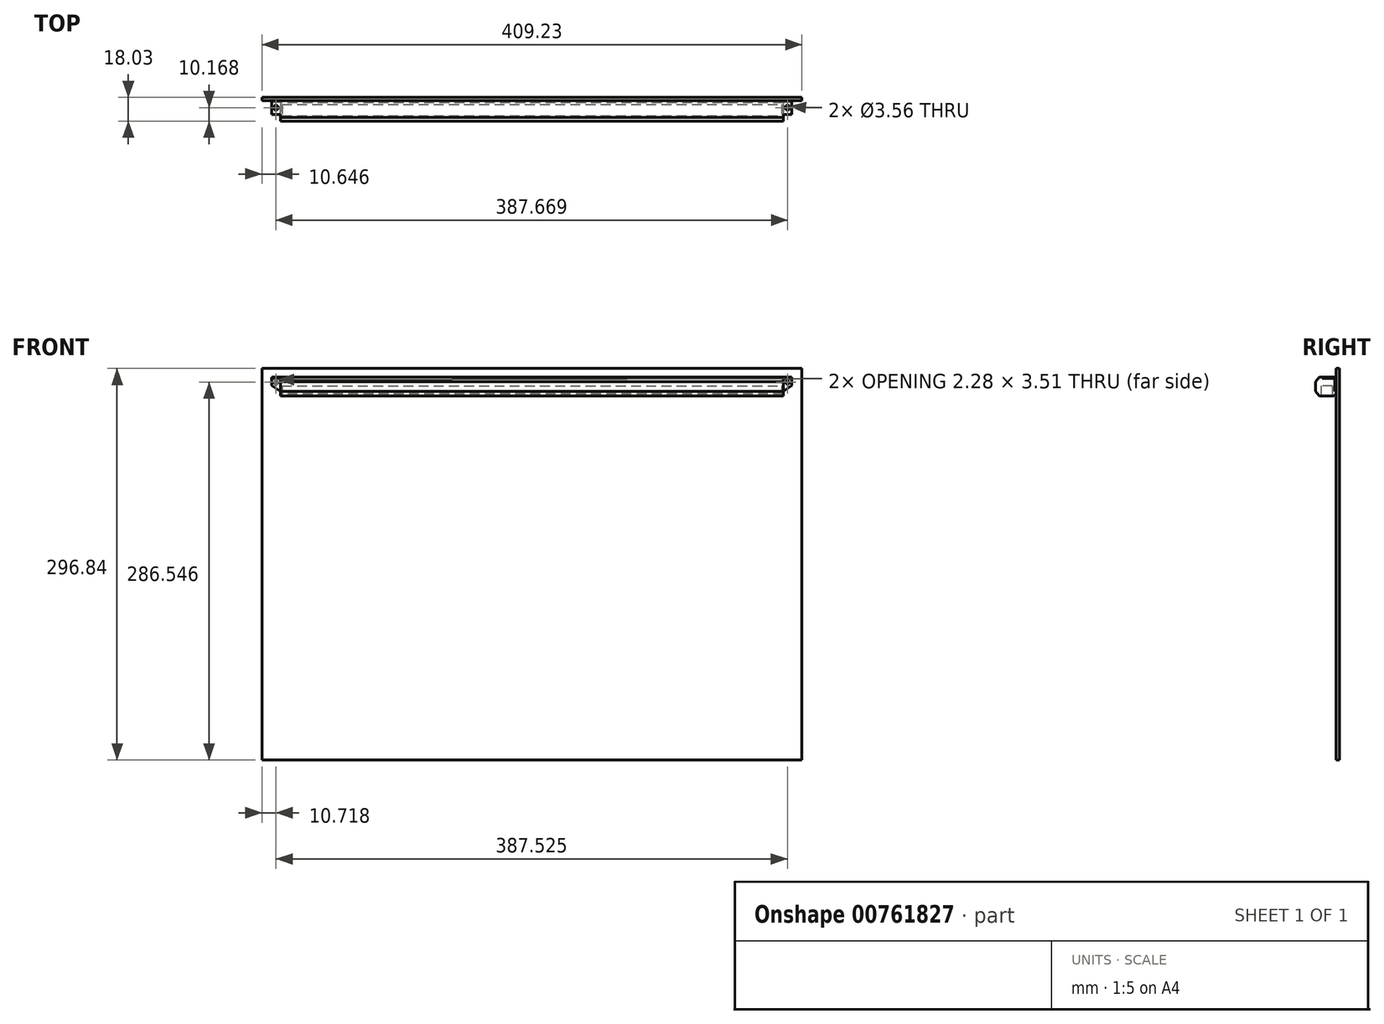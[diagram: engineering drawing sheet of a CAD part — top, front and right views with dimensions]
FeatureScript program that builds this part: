
annotation { "Feature Type Name" : "Feature", "Feature Type Description" : "" }
export const myFeature = defineFeature(function(context is Context, id is Id, definition is map)
    precondition{}
    {
        {
            var Q0;
            Q0=qCreatedBy(makeId("Right.planeOp"),FACE);
            var sketch = newSketch(context, id + "F0", { "sketchPlane" : qUnion([Q0])});
            skLineSegment(sketch, "E0", {"start": v(0, 0) * mm, "end": v(-12.7, 0) * mm});
            skLineSegment(sketch, "E1", {"start": v(0, 0) * mm, "end": v(0, -12.7) * mm});
            skLineSegment(sketch, "E2", {"start": v(-12.7, 0) * mm, "end": v(-15.49, -3.6) * mm});
            skLineSegment(sketch, "E3", {"start": v(-15.49, -3.6) * mm, "end": v(-15.49, -10.83) * mm});
            skLineSegment(sketch, "E4", {"start": v(-15.49, -10.83) * mm, "end": v(-12.7, -14.28) * mm});
            skLineSegment(sketch, "E5", {"start": v(-12.7, -14.28) * mm, "end": v(-1.49, -14.28) * mm});
            skLineSegment(sketch, "E6", {"start": v(-1.49, -14.28) * mm, "end": v(0, -12.7) * mm});
            skSolve(sketch);
        }
        {
            var Q0;
            Q0 = qSketchRegion(id + "F0", true);
            extrude(context, id + "F1", {"entities" : qUnion([Q0]), "endBound" : BoundingType.SYMMETRIC, "depth" : 381 * mm, "offsetDistance" : 25.4 * mm});
        }
        {
            var Q0;
            Q0=makeQuery(id+"F1.opExtrude","SWEPT_FACE",FACE,{"disambiguationData":[OSD([sQuery(id+"F0.wireOp",EDGE,"E5")])]});
            var sketch = newSketch(context, id + "F2", { "sketchPlane" : qUnion([Q0])});
            skLineSegment(sketch, "E7.bottom", {"start": v(-189.23, 2.76) * mm, "end": v(189.23, 2.76) * mm});
            skLineSegment(sketch, "E7.top", {"start": v(-189.23, 11.43) * mm, "end": v(189.23, 11.43) * mm});
            skLineSegment(sketch, "E7.left", {"start": v(-189.23, 2.76) * mm, "end": v(-189.23, 11.43) * mm});
            skLineSegment(sketch, "E7.right", {"start": v(189.23, 2.76) * mm, "end": v(189.23, 11.43) * mm});
            skSolve(sketch);
        }
        {
            var Q0;
            Q0 = qSketchRegion(id + "F2", true);
            extrude(context, id + "F3", {"entities" : qUnion([Q0]), "operationType" : NewBodyOperationType.REMOVE, "oppositeDirection" : true, "depth" : 7.62 * mm, "offsetDistance" : 25.4 * mm});
        }
        {
            var Q0;
            Q0=makeQuery(id+"F1.opExtrude","SWEPT_FACE",FACE,{"disambiguationData":[OSD([sQuery(id+"F0.wireOp",EDGE,"E1")])]});
            var sketch = newSketch(context, id + "F4", { "sketchPlane" : qUnion([Q0])});
            skLineSegment(sketch, "E8", {"start": v(0, 50.54) * mm, "end": v(0, -59.6) * mm, "construction": true});
            skSolve(sketch);
        }
        {
            var Q0;
            {var subQ0=sQuery(id+"F0.wireOp",EDGE,"E1");Q0=makeQuery(id+"F4.imprint","IMPRINT",FACE,{"disambiguationData":[TD([[makeQuery(id+"F4.imprint","IMPRINT",EDGE,{"derivedFrom":makeQuery(id+"F1.opExtrude","CAP_EDGE",EDGE,{"disambiguationData":[OSD([subQ0])],"isStart":true})}),-1.0]])]});}
            var sketch = newSketch(context, id + "F5", { "sketchPlane" : qUnion([Q0])});
            skLineSegment(sketch, "E9", {"start": v(-189.74, 0) * mm, "end": v(-197.1, 0) * mm});
            skLineSegment(sketch, "E10", {"start": v(-197.1, 0) * mm, "end": v(-197.1, -6.5) * mm});
            skLineSegment(sketch, "E11", {"start": v(-197.1, -6.5) * mm, "end": v(-189.74, -11.42) * mm});
            skLineSegment(sketch, "E12", {"start": v(-189.74, -11.42) * mm, "end": v(-189.74, 0) * mm});
            skPoint(sketch, "E13.orphan", {"position": v(-184.06, 0) * mm});
            skArc(sketch, "E14", {"start": v(-194.29, -3.34) * mm, "mid": v(-193.76, -5.56) * mm, "end": v(-193.25, -3.34) * mm});
            skEllipticalArc(sketch, "E15", {});
            skLineSegment(sketch, "E16.MirrorCS", {"start": v(189.74, -11.42) * mm, "end": v(189.74, 0) * mm});
            skLineSegment(sketch, "E17.MirrorCS", {"start": v(189.74, 0) * mm, "end": v(197.1, 0) * mm});
            skLineSegment(sketch, "E18.MirrorCS", {"start": v(197.1, 0) * mm, "end": v(197.1, -6.5) * mm});
            skEllipticalArc(sketch, "E19.MirrorCS", {});
            skArc(sketch, "E20.MirrorCS", {"start": v(194.29, -3.34) * mm, "mid": v(193.76, -5.56) * mm, "end": v(193.25, -3.34) * mm});
            skLineSegment(sketch, "E21.MirrorCS", {"start": v(197.1, -6.5) * mm, "end": v(189.74, -11.42) * mm});
            const initialGuessF5  = {"E15": [-0.1937689565653784, -0.0032186462401638445, 0.004613384412385034, -0.9999893582855087, 0.0011710424871544905, 0.0005225210116577835, 1.4667403996432047, 4.816444907536388], "E19.MirrorCS": [0.1937689565653784, -0.0032186462401638445, -0.004613384412385034, -0.9999893582855087, 0.0011710424871544905, 0.0005225210116577835, 1.4667403996431991, 4.816444907536382]};
            skSetInitialGuess(sketch, initialGuessF5);
            skSolve(sketch);
        }
        {
            var Q0;
            Q0 = qSketchRegion(id + "F5", true);
            extrude(context, id + "F6", {"entities" : qUnion([Q0]), "operationType" : NewBodyOperationType.ADD, "oppositeDirection" : true, "depth" : 1.02 * mm, "offsetDistance" : 25.4 * mm});
        }
        {
            var Q0;
            Q0=makeQuery(id+"F6.boolean.opBoolean","MERGE",FACE,{"derivedFrom":[makeQuery(id+"F1.opExtrude","SWEPT_FACE",FACE,{"disambiguationData":[OSD([sQuery(id+"F0.wireOp",EDGE,"E0")])]}),makeQuery(id+"F6.opExtrude","SWEPT_FACE",FACE,{"disambiguationData":[OSD([sQuery(id+"F5.wireOp",EDGE,"E9")])]}),makeQuery(id+"F6.opExtrude","SWEPT_FACE",FACE,{"disambiguationData":[OSD([sQuery(id+"F5.wireOp",EDGE,"E17.MirrorCS")])]})]});
            var sketch = newSketch(context, id + "F7", { "sketchPlane" : qUnion([Q0])});
            skLineSegment(sketch, "E22", {"start": v(0, 25.04) * mm, "end": v(0, -58.9) * mm, "construction": true});
            skSolve(sketch);
        }
        {
            var Q0;
            Q0=makeQuery(id+"F6.boolean.opBoolean","MERGE",FACE,{"derivedFrom":[makeQuery(id+"F1.opExtrude","SWEPT_FACE",FACE,{"disambiguationData":[OSD([sQuery(id+"F0.wireOp",EDGE,"E0")])]}),makeQuery(id+"F6.opExtrude","SWEPT_FACE",FACE,{"disambiguationData":[OSD([sQuery(id+"F5.wireOp",EDGE,"E9")])]}),makeQuery(id+"F6.opExtrude","SWEPT_FACE",FACE,{"disambiguationData":[OSD([sQuery(id+"F5.wireOp",EDGE,"E17.MirrorCS")])]})]});
            var sketch = newSketch(context, id + "F8", { "sketchPlane" : qUnion([Q0])});
            skLineSegment(sketch, "E23.bottom", {"start": v(197.1, 0) * mm, "end": v(190.5, 0) * mm});
            skLineSegment(sketch, "E23.top", {"start": v(197.1, -10.64) * mm, "end": v(190.5, -10.64) * mm});
            skLineSegment(sketch, "E23.left", {"start": v(197.1, 0) * mm, "end": v(197.1, -10.64) * mm});
            skLineSegment(sketch, "E23.right", {"start": v(190.5, 0) * mm, "end": v(190.5, -10.64) * mm});
            skCircle(sketch, "E24", {"center": v(193.83, -5.32) * mm, "radius": 1.78 * mm});
            skPoint(sketch, "E24.centerSnap0", {"position": v(197.1, -5.32) * mm});
            skLineSegment(sketch, "E25.MirrorCS", {"start": v(-197.1, -10.64) * mm, "end": v(-190.5, -10.64) * mm});
            skLineSegment(sketch, "E26.MirrorCS", {"start": v(-190.5, 0) * mm, "end": v(-190.5, -10.64) * mm});
            skLineSegment(sketch, "E27.MirrorCS", {"start": v(-197.1, 0) * mm, "end": v(-190.5, 0) * mm});
            skLineSegment(sketch, "E28.MirrorCS", {"start": v(-197.1, 0) * mm, "end": v(-197.1, -10.64) * mm});
            skCircle(sketch, "E29.MirrorC", {"center": v(-193.83, -5.32) * mm, "radius": 1.78 * mm});
            skSolve(sketch);
        }
        {
            var Q0;
            Q0 = qSketchRegion(id + "F8", true);
            extrude(context, id + "F9", {"entities" : qUnion([Q0]), "operationType" : NewBodyOperationType.ADD, "oppositeDirection" : true, "depth" : 1.02 * mm, "offsetDistance" : 25.4 * mm});
        }
        {
            var Q0;
            Q0=qCreatedBy(makeId("Front.planeOp"),FACE);
            cPlane(context, id + "F10", {"entities" : qUnion([Q0]), "cplaneType" : CPlaneType.OFFSET, "offset" : 0 * mm, "oppositeDirection" : true, "width" : 152.4 * mm, "height" : 152.4 * mm});
        }
        {
            var Q0;
            Q0=qCreatedBy(id+"F10.planeOp",FACE);
            var sketch = newSketch(context, id + "F11", { "sketchPlane" : qUnion([Q0])});
            skLineSegment(sketch, "E30.bottom", {"start": v(-204.48, 6.49) * mm, "end": v(204.75, 6.49) * mm});
            skLineSegment(sketch, "E30.top", {"start": v(-204.48, -290.35) * mm, "end": v(204.75, -290.35) * mm});
            skLineSegment(sketch, "E30.left", {"start": v(-204.48, 6.49) * mm, "end": v(-204.48, -290.35) * mm});
            skLineSegment(sketch, "E30.right", {"start": v(204.75, 6.49) * mm, "end": v(204.75, -290.35) * mm});
            skSolve(sketch);
        }
        {
            var Q0;
            Q0 = qSketchRegion(id + "F11", true);
            extrude(context, id + "F12", {"entities" : qUnion([Q0]), "oppositeDirection" : true, "depth" : 2.54 * mm, "offsetDistance" : 25.4 * mm});
        }
    });
